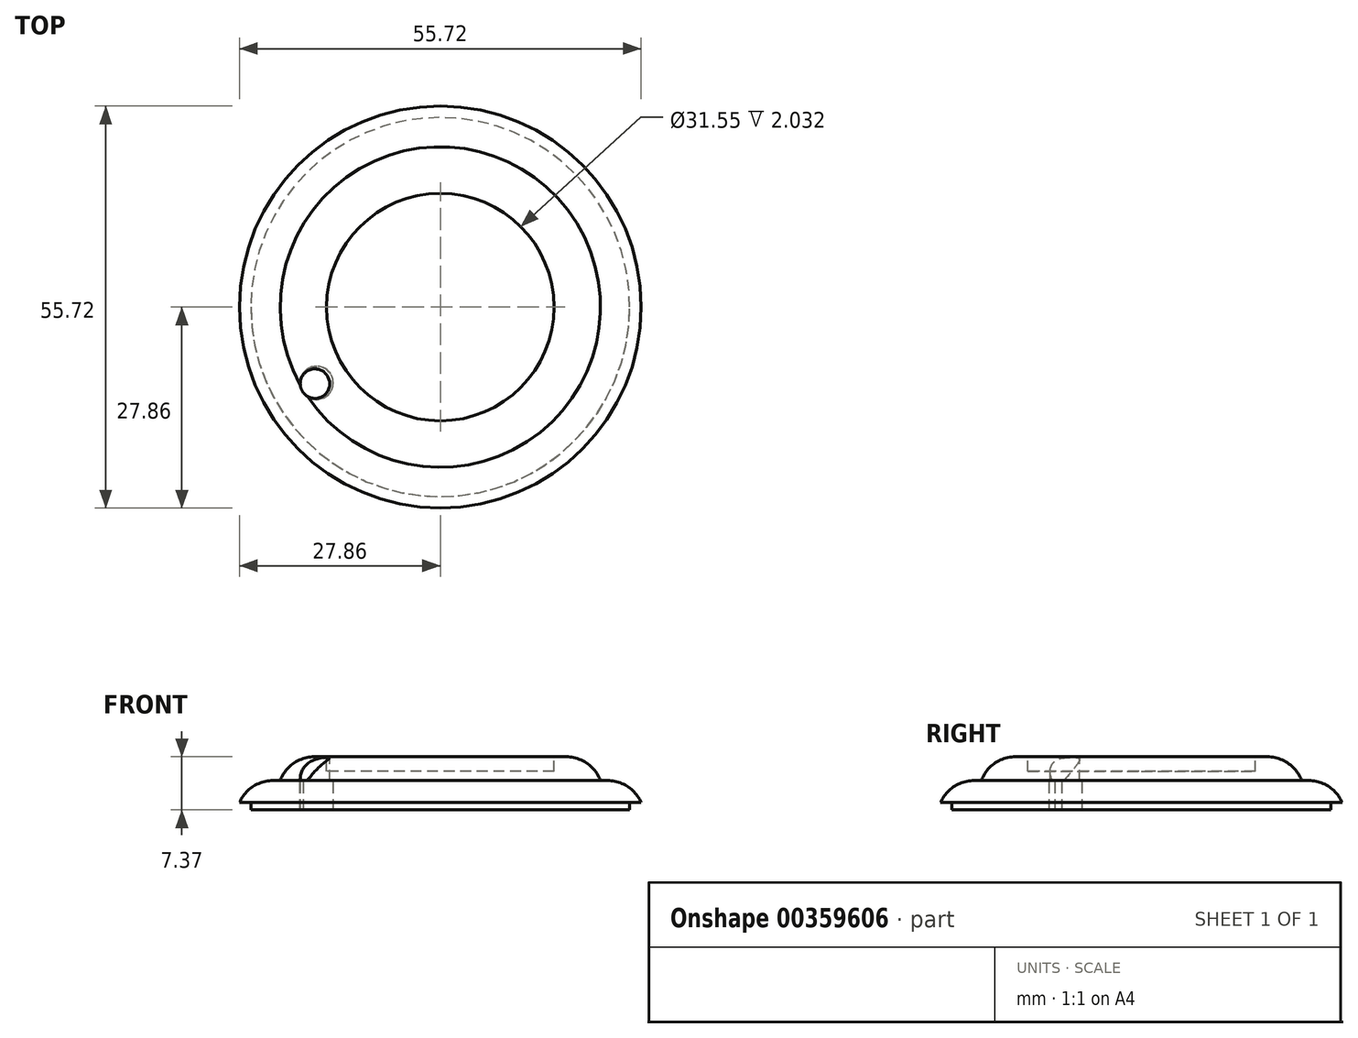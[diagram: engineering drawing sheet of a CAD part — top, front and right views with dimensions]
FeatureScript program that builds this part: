
annotation { "Feature Type Name" : "Feature", "Feature Type Description" : "" }
export const myFeature = defineFeature(function(context is Context, id is Id, definition is map)
    precondition{}
    {
        {
            var Q0;
            Q0=qCreatedBy(makeId("Top.planeOp"),FACE);
            var sketch = newSketch(context, id + "F0", { "sketchPlane" : qUnion([Q0])});
            skCircle(sketch, "E0", {"center": v(0, 0) * mm, "radius": 27.86 * mm});
            skSolve(sketch);
        }
        {
            var Q0;
            Q0=makeQuery(id+"F0.imprint","IMPRINT",FACE,{"disambiguationData":[TD([[makeQuery(id+"F0.imprint","IMPRINT",EDGE,{"derivedFrom":sQuery(id+"F0.wireOp",EDGE,"E0")}),1.0]])]});
            extrude(context, id + "F1", {"entities" : qUnion([Q0]), "depth" : 3.05 * mm});
        }
        {
            var Q0;
            Q0=makeQuery(id+"F1.opExtrude","CAP_EDGE",EDGE,{"disambiguationData":[OSD([sQuery(id+"F0.wireOp",EDGE,"E0")])],"isStart":false});
            fillet(context, id + "F2", {"entities" : qUnion([Q0]), "radius" : 5.08 * mm, "tangentPropagation" : true, "allowEdgeOverflow" : false});
        }
        {
            var Q0;
            Q0=makeQuery(id+"F1.opExtrude","CAP_FACE",FACE,{"disambiguationData":[OSD([sQuery(id+"F0.wireOp",EDGE,"E0")])],"isStart":true});
            var sketch = newSketch(context, id + "F3", { "sketchPlane" : qUnion([Q0])});
            skSolve(sketch);
        }
        {
            var Q0;
            {var subQ0=sQuery(id+"F0.wireOp",EDGE,"E0");Q0=makeQuery(id+"F3.imprint","IMPRINT",FACE,{"disambiguationData":[TD([[makeQuery(id+"F3.imprint","IMPRINT",EDGE,{"derivedFrom":makeQuery(id+"F2.opFillet","BLEND_EDGE",EDGE,{"blendedFrom":[makeQuery(id+"F1.opExtrude","CAP_EDGE",EDGE,{"disambiguationData":[OSD([subQ0])],"isStart":false}),makeQuery(id+"F1.opExtrude","CAP_FACE",FACE,{"disambiguationData":[OSD([subQ0])],"isStart":true})],"blendedInto":[makeQuery(id+"F1.opExtrude","CAP_FACE",FACE,{"disambiguationData":[OSD([subQ0])],"isStart":true})]})}),-1.0]])]});}
            var sketch = newSketch(context, id + "F4", { "sketchPlane" : qUnion([Q0])});
            skCircle(sketch, "E1", {"center": v(0, 0) * mm, "radius": 26.28 * mm});
            skSolve(sketch);
        }
        {
            var Q0;
            Q0=qSketchRegion(id+"F4",true);
            extrude(context, id + "F5", {"entities" : qUnion([Q0]), "operationType" : NewBodyOperationType.ADD, "depth" : 1.02 * mm});
        }
        {
            var Q0;
            Q0=makeQuery(id+"F1.opExtrude","CAP_FACE",FACE,{"disambiguationData":[OSD([sQuery(id+"F0.wireOp",EDGE,"E0")])],"isStart":false});
            var sketch = newSketch(context, id + "F6", { "sketchPlane" : qUnion([Q0])});
            skCircle(sketch, "E2", {"center": v(0, 0) * mm, "radius": 22.22 * mm});
            skSolve(sketch);
        }
        {
            var Q0;
            Q0=makeQuery(id+"F6.imprint","IMPRINT",FACE,{"disambiguationData":[TD([[makeQuery(id+"F6.imprint","IMPRINT",EDGE,{"derivedFrom":sQuery(id+"F6.wireOp",EDGE,"E2")}),1.0]])]});
            extrude(context, id + "F7", {"entities" : qUnion([Q0]), "operationType" : NewBodyOperationType.ADD, "depth" : 3.3 * mm});
        }
        {
            var Q0;
            Q0=makeQuery(id+"F7.opExtrude","CAP_EDGE",EDGE,{"disambiguationData":[OSD([sQuery(id+"F6.wireOp",EDGE,"E2")])],"isStart":false});
            fillet(context, id + "F8", {"entities" : qUnion([Q0]), "radius" : 5.08 * mm, "tangentPropagation" : true, "allowEdgeOverflow" : false});
        }
        {
            var Q0;
            Q0=makeQuery(id+"F7.opExtrude","CAP_FACE",FACE,{"disambiguationData":[OSD([sQuery(id+"F6.wireOp",EDGE,"E2")])],"isStart":false});
            var sketch = newSketch(context, id + "F9", { "sketchPlane" : qUnion([Q0])});
            skCircle(sketch, "E3", {"center": v(0, 0) * mm, "radius": 15.77 * mm});
            skSolve(sketch);
        }
        {
            var Q0;
            Q0=makeQuery(id+"F9.imprint","IMPRINT",FACE,{"disambiguationData":[TD([[makeQuery(id+"F9.imprint","IMPRINT",EDGE,{"derivedFrom":sQuery(id+"F9.wireOp",EDGE,"E3")}),1.0]])]});
            extrude(context, id + "F10", {"entities" : qUnion([Q0]), "operationType" : NewBodyOperationType.REMOVE, "oppositeDirection" : true, "depth" : 2.03 * mm});
        }
        {
            var Q0;
            Q0=makeQuery(id+"F1.opExtrude","CAP_FACE",FACE,{"disambiguationData":[OSD([sQuery(id+"F0.wireOp",EDGE,"E0")])],"isStart":false});
            var sketch = newSketch(context, id + "F11", { "sketchPlane" : qUnion([Q0])});
            skCircle(sketch, "E4", {"center": v(-17.16, -10.5) * mm, "radius": 2.3 * mm});
            skSolve(sketch);
        }
        {
            var Q0;
            Q0=qSketchRegion(id+"F11",true);
            extrude(context, id + "F12", {"entities" : qUnion([Q0]), "operationType" : NewBodyOperationType.REMOVE, "oppositeDirection" : true, "depth" : 21.34 * mm});
        }
        {
            var Q0;
            Q0=makeQuery(id+"F7.opExtrude","CAP_FACE",FACE,{"disambiguationData":[OSD([sQuery(id+"F6.wireOp",EDGE,"E2")])],"isStart":false});
            var sketch = newSketch(context, id + "F13", { "sketchPlane" : qUnion([Q0])});
            skCircle(sketch, "E5", {"center": v(-17.39, -10.62) * mm, "radius": 2.05 * mm});
            skSolve(sketch);
        }
        {
            var Q0;
            Q0=qSketchRegion(id+"F13",true);
            extrude(context, id + "F14", {"entities" : qUnion([Q0]), "operationType" : NewBodyOperationType.REMOVE, "oppositeDirection" : true, "depth" : 25.4 * mm});
        }
    });
